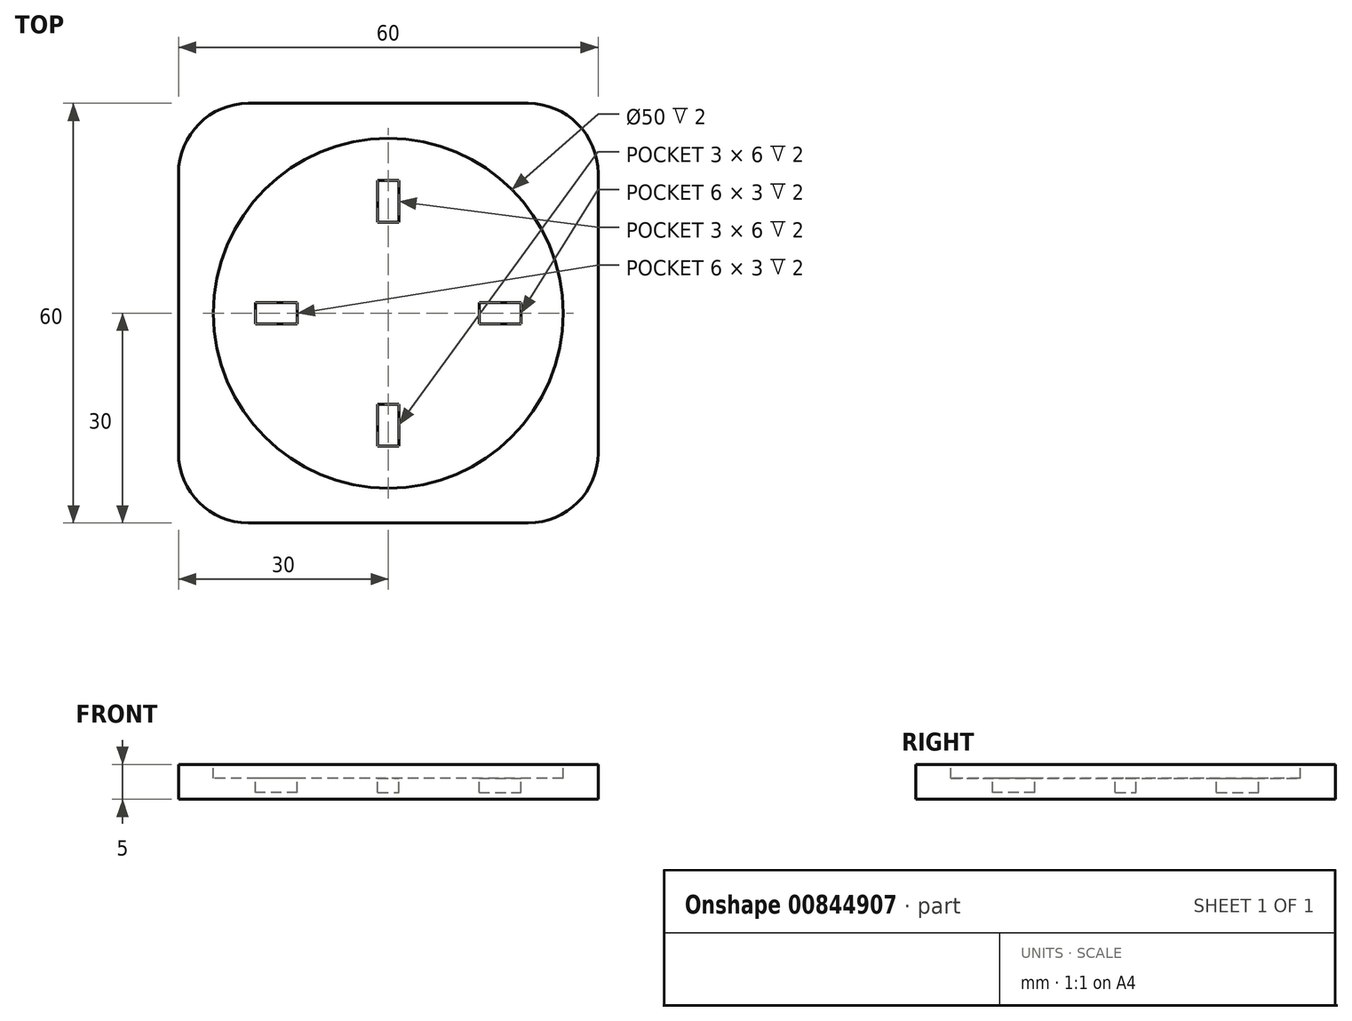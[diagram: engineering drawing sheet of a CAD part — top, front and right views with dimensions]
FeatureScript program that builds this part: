
annotation { "Feature Type Name" : "Feature", "Feature Type Description" : "" }
export const myFeature = defineFeature(function(context is Context, id is Id, definition is map)
    precondition{}
    {
        {
            var Q0;
            Q0=qCreatedBy(makeId("Top.planeOp"),FACE);
            var sketch = newSketch(context, id + "F0", { "sketchPlane" : qUnion([Q0])});
            skLineSegment(sketch, "E0.bottom", {"start": v(30, -30) * mm, "end": v(-30, -30) * mm});
            skLineSegment(sketch, "E0.top", {"start": v(30, 30) * mm, "end": v(-30, 30) * mm});
            skLineSegment(sketch, "E0.left", {"start": v(30, -30) * mm, "end": v(30, 30) * mm});
            skLineSegment(sketch, "E0.right", {"start": v(-30, -30) * mm, "end": v(-30, 30) * mm});
            skPoint(sketch, "E0.middle", {"position": v(0, 0) * mm});
            skSolve(sketch);
        }
        {
            var Q0;
            Q0=makeQuery(id+"F0.imprint","IMPRINT",FACE,{"disambiguationData":[TD([[makeQuery(id+"F0.imprint","IMPRINT",EDGE,{"derivedFrom":sQuery(id+"F0.wireOp",EDGE,"E0.bottom")}),-1.0]])]});
            extrude(context, id + "F1", {"entities" : qUnion([Q0]), "depth" : 5 * mm, "offsetDistance" : 25 * mm});
        }
        {
            var Q0;
            Q0=makeQuery(id+"F1.opExtrude","CAP_FACE",FACE,{"disambiguationData":[OSD([sQuery(id+"F0.wireOp",EDGE,"E0.bottom"),sQuery(id+"F0.wireOp",EDGE,"E0.top"),sQuery(id+"F0.wireOp",EDGE,"E0.left"),sQuery(id+"F0.wireOp",EDGE,"E0.right")])],"isStart":false});
            var sketch = newSketch(context, id + "F2", { "sketchPlane" : qUnion([Q0])});
            skCircle(sketch, "E1", {"center": v(0, 0) * mm, "radius": 25 * mm});
            skSolve(sketch);
        }
        {
            var Q0;
            Q0=makeQuery(id+"F2.imprint","IMPRINT",FACE,{"disambiguationData":[TD([[makeQuery(id+"F2.imprint","IMPRINT",EDGE,{"derivedFrom":sQuery(id+"F2.wireOp",EDGE,"E1")}),1.0]])]});
            extrude(context, id + "F3", {"entities" : qUnion([Q0]), "operationType" : NewBodyOperationType.REMOVE, "oppositeDirection" : true, "depth" : 2 * mm, "offsetDistance" : 25 * mm});
        }
        {
            var Q0;
            Q0=makeQuery(id+"F1.opExtrude","SWEPT_EDGE",EDGE,{"disambiguationData":[OSD([sQuery(id+"F0.wireOp",EDGE,"E0.bottom"),sQuery(id+"F0.wireOp",EDGE,"E0.left")])]});
            var Q1;
            Q1=makeQuery(id+"F1.opExtrude","SWEPT_EDGE",EDGE,{"disambiguationData":[OSD([sQuery(id+"F0.wireOp",EDGE,"E0.top"),sQuery(id+"F0.wireOp",EDGE,"E0.left")])]});
            var Q2;
            Q2=makeQuery(id+"F1.opExtrude","SWEPT_EDGE",EDGE,{"disambiguationData":[OSD([sQuery(id+"F0.wireOp",EDGE,"E0.top"),sQuery(id+"F0.wireOp",EDGE,"E0.right")])]});
            var Q3;
            Q3=makeQuery(id+"F1.opExtrude","SWEPT_EDGE",EDGE,{"disambiguationData":[OSD([sQuery(id+"F0.wireOp",EDGE,"E0.bottom"),sQuery(id+"F0.wireOp",EDGE,"E0.right")])]});
            fillet(context, id + "F4", {"entities" : qUnion([Q0, Q1, Q2, Q3]), "radius" : 10 * mm, "tangentPropagation" : true, "allowEdgeOverflow" : false});
        }
        {
            var Q0;
            Q0=makeQuery(id+"F3.boolean.opBoolean","COPY",FACE,{"derivedFrom":makeQuery(id+"F3.opExtrude","CAP_FACE",FACE,{"disambiguationData":[OSD([sQuery(id+"F2.wireOp",EDGE,"E1")])],"isStart":false})});
            var sketch = newSketch(context, id + "F5", { "sketchPlane" : qUnion([Q0])});
            skLineSegment(sketch, "E2.bottom", {"start": v(1.5, 13) * mm, "end": v(-1.5, 13) * mm});
            skLineSegment(sketch, "E2.top", {"start": v(1.5, 19) * mm, "end": v(-1.5, 19) * mm});
            skLineSegment(sketch, "E2.left", {"start": v(1.5, 13) * mm, "end": v(1.5, 19) * mm});
            skLineSegment(sketch, "E2.right", {"start": v(-1.5, 13) * mm, "end": v(-1.5, 19) * mm});
            skPoint(sketch, "E2.middle", {"position": v(0, 16) * mm});
            skLineSegment(sketch, "E3.1.0", {"start": v(-13, 1.5) * mm, "end": v(-19, 1.5) * mm});
            skLineSegment(sketch, "E3.1.1", {"start": v(-13, -1.5) * mm, "end": v(-19, -1.5) * mm});
            skLineSegment(sketch, "E3.1.2", {"start": v(-19, 1.5) * mm, "end": v(-19, -1.5) * mm});
            skLineSegment(sketch, "E3.1.3", {"start": v(-13, 1.5) * mm, "end": v(-13, -1.5) * mm});
            skLineSegment(sketch, "E3.2.0", {"start": v(-1.5, -13) * mm, "end": v(-1.5, -19) * mm});
            skLineSegment(sketch, "E3.2.1", {"start": v(1.5, -13) * mm, "end": v(1.5, -19) * mm});
            skLineSegment(sketch, "E3.2.2", {"start": v(-1.5, -19) * mm, "end": v(1.5, -19) * mm});
            skLineSegment(sketch, "E3.2.3", {"start": v(-1.5, -13) * mm, "end": v(1.5, -13) * mm});
            skLineSegment(sketch, "E3.3.0", {"start": v(13, -1.5) * mm, "end": v(19, -1.5) * mm});
            skLineSegment(sketch, "E3.3.1", {"start": v(13, 1.5) * mm, "end": v(19, 1.5) * mm});
            skLineSegment(sketch, "E3.3.2", {"start": v(19, -1.5) * mm, "end": v(19, 1.5) * mm});
            skLineSegment(sketch, "E3.3.3", {"start": v(13, -1.5) * mm, "end": v(13, 1.5) * mm});
            skPoint(sketch, "E3.center", {"position": v(0, 0) * mm});
            skSolve(sketch);
        }
        {
            var Q0;
            Q0=makeQuery(id+"F5.imprint","IMPRINT",FACE,{"disambiguationData":[TD([[makeQuery(id+"F5.imprint","IMPRINT",EDGE,{"derivedFrom":sQuery(id+"F5.wireOp",EDGE,"E3.1.0")}),1.0]])]});
            var Q1;
            Q1=makeQuery(id+"F5.imprint","IMPRINT",FACE,{"disambiguationData":[TD([[makeQuery(id+"F5.imprint","IMPRINT",EDGE,{"derivedFrom":sQuery(id+"F5.wireOp",EDGE,"E2.bottom")}),-1.0]])]});
            var Q2;
            Q2=makeQuery(id+"F5.imprint","IMPRINT",FACE,{"disambiguationData":[TD([[makeQuery(id+"F5.imprint","IMPRINT",EDGE,{"derivedFrom":sQuery(id+"F5.wireOp",EDGE,"E3.3.0")}),1.0]])]});
            var Q3;
            Q3=makeQuery(id+"F5.imprint","IMPRINT",FACE,{"disambiguationData":[TD([[makeQuery(id+"F5.imprint","IMPRINT",EDGE,{"derivedFrom":sQuery(id+"F5.wireOp",EDGE,"E3.2.0")}),1.0]])]});
            extrude(context, id + "F6", {"entities" : qUnion([Q0, Q1, Q2, Q3]), "operationType" : NewBodyOperationType.REMOVE, "oppositeDirection" : true, "depth" : 2 * mm, "offsetDistance" : 25 * mm});
        }
    });
